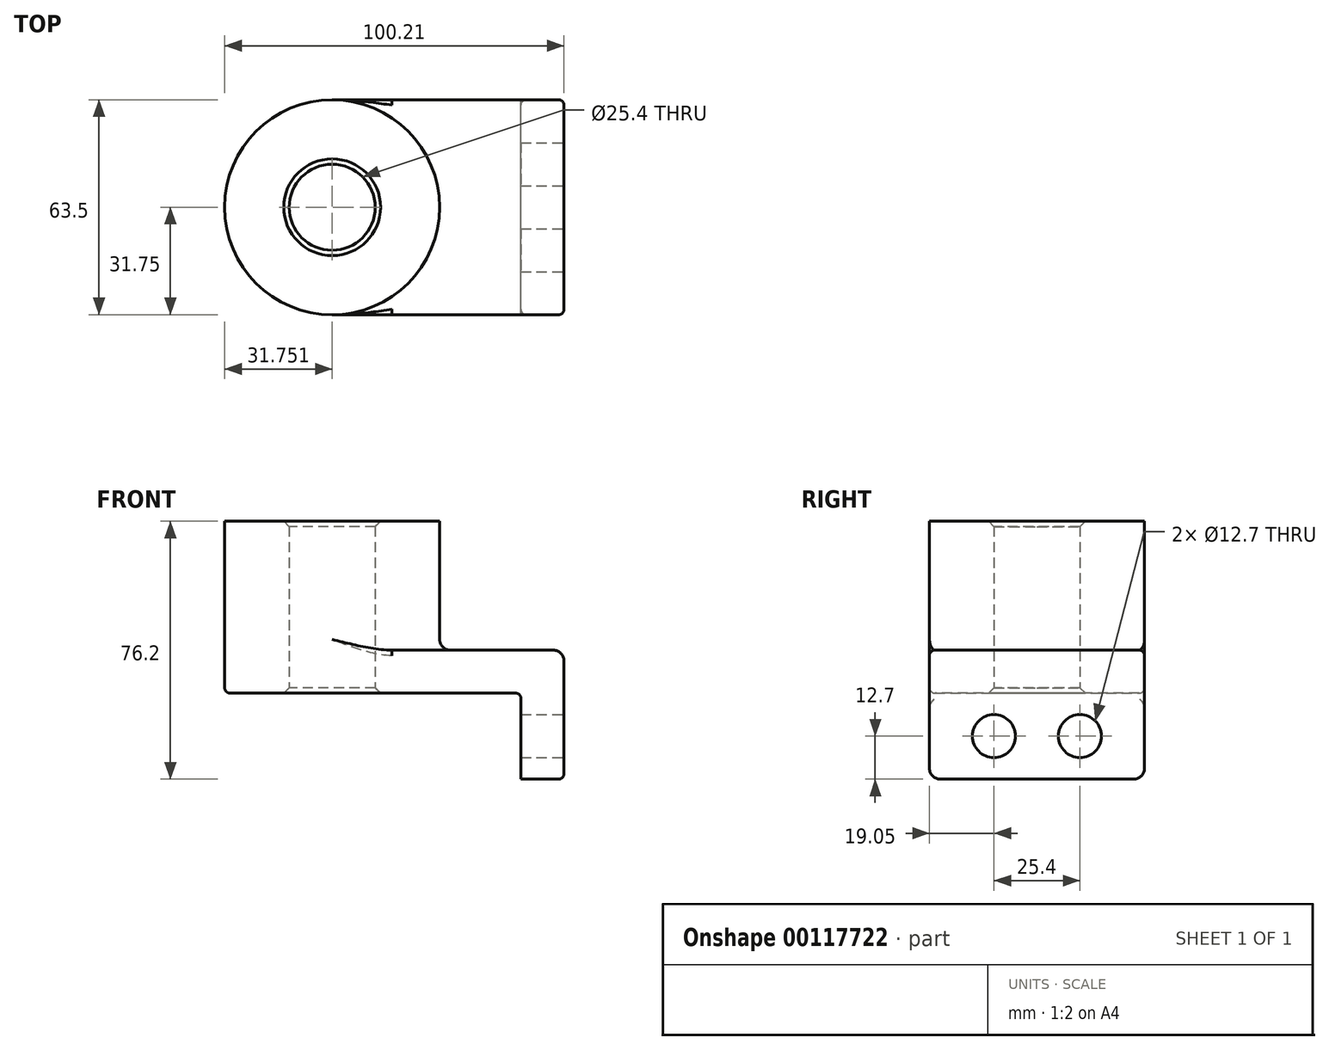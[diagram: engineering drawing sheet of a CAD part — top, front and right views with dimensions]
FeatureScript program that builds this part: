
annotation { "Feature Type Name" : "Feature", "Feature Type Description" : "" }
export const myFeature = defineFeature(function(context is Context, id is Id, definition is map)
    precondition{}
    {
        {
            var Q0;
            Q0=qCreatedBy(makeId("Top.planeOp"),FACE);
            var sketch = newSketch(context, id + "F0", { "sketchPlane" : qUnion([Q0])});
            skLineSegment(sketch, "E0.bottom", {"start": v(-34.23, 31.75) * mm, "end": v(34.23, 31.75) * mm});
            skLineSegment(sketch, "E0.top", {"start": v(-34.23, -31.75) * mm, "end": v(34.23, -31.75) * mm});
            skLineSegment(sketch, "E0.left", {"start": v(-34.23, 31.75) * mm, "end": v(-34.23, -31.75) * mm});
            skLineSegment(sketch, "E0.right", {"start": v(34.23, 31.75) * mm, "end": v(34.23, -31.75) * mm});
            skPoint(sketch, "E0.middle", {"position": v(0, 0) * mm});
            skCircle(sketch, "E1", {"center": v(-34.23, 0) * mm, "radius": 31.75 * mm});
            skCircle(sketch, "E2", {"center": v(-34.23, 0) * mm, "radius": 12.7 * mm});
            skSolve(sketch);
        }
        {
            var Q0;
            Q0 = qSketchRegion(id + "F0", true);
            extrude(context, id + "F1", {"entities" : qUnion([Q0]), "depth" : 12.7 * mm});
        }
        {
            var Q0;
            Q0=makeQuery(id+"F1.opExtrude","SWEPT_FACE",FACE,{"disambiguationData":[OSD([sQuery(id+"F0.wireOp",EDGE,"E0.right")])]});
            var sketch = newSketch(context, id + "F2", { "sketchPlane" : qUnion([Q0])});
            skLineSegment(sketch, "E3.bottom", {"start": v(-31.75, 12.7) * mm, "end": v(31.75, 12.7) * mm});
            skLineSegment(sketch, "E3.top", {"start": v(-31.75, -25.4) * mm, "end": v(31.75, -25.4) * mm});
            skLineSegment(sketch, "E3.left", {"start": v(-31.75, 12.7) * mm, "end": v(-31.75, -25.4) * mm});
            skLineSegment(sketch, "E3.right", {"start": v(31.75, 12.7) * mm, "end": v(31.75, -25.4) * mm});
            skCircle(sketch, "E4", {"center": v(-12.7, -12.7) * mm, "radius": 6.35 * mm});
            skLineSegment(sketch, "E5", {"start": v(0, 0) * mm, "end": v(0, -25.4) * mm});
            skCircle(sketch, "E6.MirrorC", {"center": v(12.7, -12.7) * mm, "radius": 6.35 * mm});
            skSolve(sketch);
        }
        {
            var Q0;
            Q0 = qSketchRegion(id + "F2", true);
            extrude(context, id + "F3", {"entities" : qUnion([Q0]), "operationType" : NewBodyOperationType.ADD, "oppositeDirection" : true, "depth" : 12.7 * mm});
        }
        {
            var Q0;
            {var subQ1=sQuery(id+"F0.wireOp",EDGE,"E0.left");var subQ3=sQuery(id+"F0.wireOp",EDGE,"E2");var subQ4=makeQuery(id+"F0.imprint","INTERSECT",VERTEX,{"disambiguationData":[OD(0.0)],"derivedFrom":[subQ1,subQ3]});Q0=makeQuery(id+"F0.imprint","IMPRINT",FACE,{"disambiguationData":[TD([[makeQuery(id+"F0.imprint","IMPRINT",EDGE,{"disambiguationData":[TD([[subQ4,1.0]])],"derivedFrom":subQ3}),-1.0]])]});}
            var Q1;
            {var subQ1=sQuery(id+"F0.wireOp",EDGE,"E0.left");var subQ3=sQuery(id+"F0.wireOp",EDGE,"E2");var subQ4=makeQuery(id+"F0.imprint","INTERSECT",VERTEX,{"disambiguationData":[OD(0.0)],"derivedFrom":[subQ1,subQ3]});Q1=makeQuery(id+"F0.imprint","IMPRINT",FACE,{"disambiguationData":[TD([[makeQuery(id+"F0.imprint","IMPRINT",EDGE,{"disambiguationData":[TD([[subQ4,-1.0]])],"derivedFrom":subQ3}),-1.0]])]});}
            extrude(context, id + "F4", {"entities" : qUnion([Q0, Q1]), "operationType" : NewBodyOperationType.ADD, "depth" : 50.8 * mm});
        }
        {
            var Q0;
            {var subQ0=sQuery(id+"F0.wireOp",EDGE,"E1");Q0=makeQuery(id+"F4.boolean.opBoolean","INTERSECT",EDGE,{"derivedFrom":[makeQuery(id+"F1.opExtrude","CAP_FACE",FACE,{"disambiguationData":[OSD([sQuery(id+"F0.wireOp",EDGE,"E0.bottom"),sQuery(id+"F0.wireOp",EDGE,"E0.top"),sQuery(id+"F0.wireOp",EDGE,"E0.right"),subQ0,sQuery(id+"F0.wireOp",EDGE,"E2")])],"isStart":false}),makeQuery(id+"F4.opExtrude","SWEPT_FACE",FACE,{"disambiguationData":[OSD([subQ0])]})]});}
            var Q1;
            Q1=makeQuery(id+"F1.opExtrude","CAP_EDGE",EDGE,{"disambiguationData":[OSD([sQuery(id+"F0.wireOp",EDGE,"E0.right")])],"isStart":false});
            var Q2;
            Q2=makeQuery(id+"F3.opExtrude","SWEPT_EDGE",EDGE,{"disambiguationData":[OSD([sQuery(id+"F2.wireOp",EDGE,"E3.top"),sQuery(id+"F2.wireOp",EDGE,"E3.left")])]});
            var Q3;
            Q3=makeQuery(id+"F3.opExtrude","SWEPT_EDGE",EDGE,{"disambiguationData":[OSD([sQuery(id+"F2.wireOp",EDGE,"E3.top"),sQuery(id+"F2.wireOp",EDGE,"E3.right")])]});
            fillet(context, id + "F5", {"entities" : qUnion([Q0, Q1, Q2, Q3]), "radius" : 3.17 * mm, "tangentPropagation" : true, "allowEdgeOverflow" : false});
        }
        {
            var Q0;
            Q0=makeQuery(id+"F1.opExtrude","CAP_EDGE",EDGE,{"disambiguationData":[OSD([sQuery(id+"F0.wireOp",EDGE,"E0.top")])],"isStart":true});
            var Q1;
            Q1=makeQuery(id+"F3.boolean.opBoolean","INTERSECT",EDGE,{"derivedFrom":[makeQuery(id+"F1.opExtrude","CAP_FACE",FACE,{"disambiguationData":[OSD([sQuery(id+"F0.wireOp",EDGE,"E0.bottom"),sQuery(id+"F0.wireOp",EDGE,"E0.top"),sQuery(id+"F0.wireOp",EDGE,"E0.right"),sQuery(id+"F0.wireOp",EDGE,"E1"),sQuery(id+"F0.wireOp",EDGE,"E2")])],"isStart":true}),makeQuery(id+"F3.opExtrude","CAP_FACE",FACE,{"disambiguationData":[OSD([sQuery(id+"F2.wireOp",EDGE,"E3.bottom"),sQuery(id+"F2.wireOp",EDGE,"E3.top"),sQuery(id+"F2.wireOp",EDGE,"E3.left"),sQuery(id+"F2.wireOp",EDGE,"E3.right"),sQuery(id+"F2.wireOp",EDGE,"E4"),sQuery(id+"F2.wireOp",EDGE,"E6.MirrorC")])],"isStart":false})]});
            var Q2;
            Q2=makeQuery(id+"F1.opExtrude","CAP_EDGE",EDGE,{"disambiguationData":[OSD([sQuery(id+"F0.wireOp",EDGE,"E0.top")])],"isStart":false});
            fillet(context, id + "F6", {"entities" : qUnion([Q0, Q1, Q2]), "radius" : 1.59 * mm, "tangentPropagation" : true, "allowEdgeOverflow" : false});
        }
        {
            var Q0;
            {var subQ0=sQuery(id+"F0.wireOp",EDGE,"E2");Q0=makeQuery(id+"F4.boolean.opBoolean","MERGE",FACE,{"derivedFrom":[makeQuery(id+"F1.opExtrude","SWEPT_FACE",FACE,{"disambiguationData":[OSD([subQ0])]}),makeQuery(id+"F4.opExtrude","SWEPT_FACE",FACE,{"disambiguationData":[OSD([subQ0])]})]});}
            chamfer(context, id + "F7", {"entities" : qUnion([Q0]), "width" : 1.59 * mm, "tangentPropagation" : true});
        }
    });
